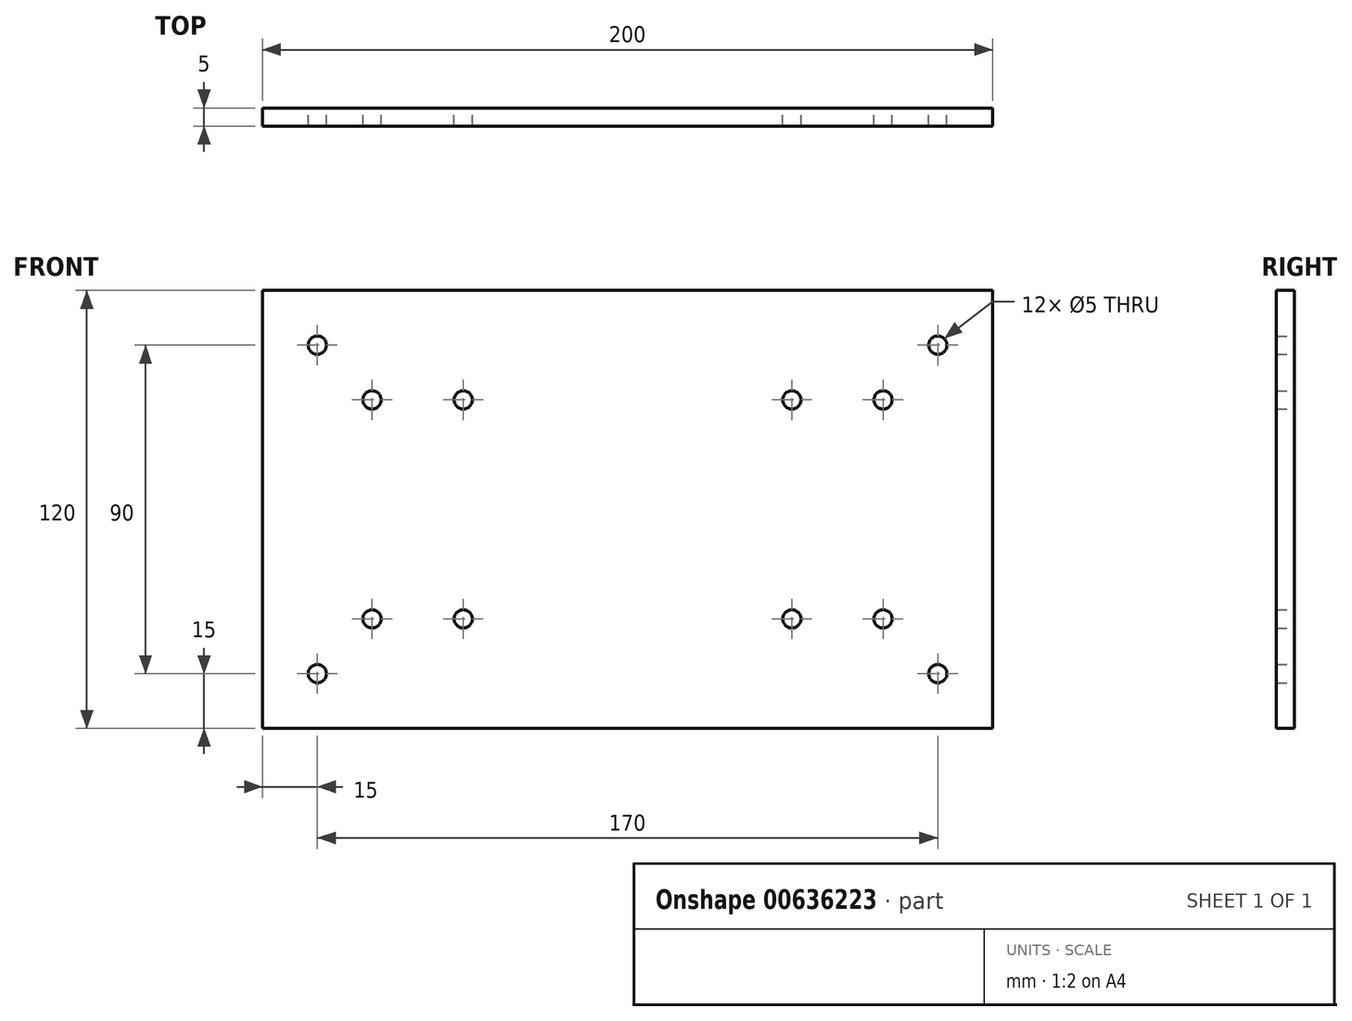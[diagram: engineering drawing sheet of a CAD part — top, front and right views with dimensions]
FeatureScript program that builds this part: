
annotation { "Feature Type Name" : "Feature", "Feature Type Description" : "" }
export const myFeature = defineFeature(function(context is Context, id is Id, definition is map)
    precondition{}
    {
        {
            var Q0;
            Q0=qCreatedBy(makeId("Front.planeOp"),FACE);
            var sketch = newSketch(context, id + "F0", { "sketchPlane" : qUnion([Q0])});
            skLineSegment(sketch, "E0.bottom", {"start": v(0, 0) * mm, "end": v(200, 0) * mm});
            skLineSegment(sketch, "E0.top", {"start": v(0, 120) * mm, "end": v(200, 120) * mm});
            skLineSegment(sketch, "E0.left", {"start": v(0, 0) * mm, "end": v(0, 120) * mm});
            skLineSegment(sketch, "E0.right", {"start": v(200, 0) * mm, "end": v(200, 120) * mm});
            skCircle(sketch, "E1", {"center": v(15, 105) * mm, "radius": 2.5 * mm});
            skCircle(sketch, "E2", {"center": v(30, 90) * mm, "radius": 2.5 * mm});
            skCircle(sketch, "E3", {"center": v(54.99, 90) * mm, "radius": 2.5 * mm});
            skCircle(sketch, "E4.MirrorC", {"center": v(185, 105) * mm, "radius": 2.5 * mm});
            skCircle(sketch, "E5.MirrorC", {"center": v(145.01, 90) * mm, "radius": 2.5 * mm});
            skCircle(sketch, "E6.MirrorC", {"center": v(170, 90) * mm, "radius": 2.5 * mm});
            skCircle(sketch, "E7.MirrorC", {"center": v(15, 15) * mm, "radius": 2.5 * mm});
            skCircle(sketch, "E8.MirrorC", {"center": v(30, 30) * mm, "radius": 2.5 * mm});
            skCircle(sketch, "E9.MirrorC", {"center": v(54.99, 30) * mm, "radius": 2.5 * mm});
            skCircle(sketch, "E10.MirrorC", {"center": v(145.01, 30) * mm, "radius": 2.5 * mm});
            skCircle(sketch, "E11.MirrorC", {"center": v(170, 30) * mm, "radius": 2.5 * mm});
            skCircle(sketch, "E12.MirrorC", {"center": v(185, 15) * mm, "radius": 2.5 * mm});
            skLineSegment(sketch, "E13", {"start": v(15, 15) * mm, "end": v(30, 30) * mm});
            skSolve(sketch);
        }
        {
            var Q0;
            Q0=makeQuery(id+"F0.imprint","IMPRINT",FACE,{"disambiguationData":[TD([[makeQuery(id+"F0.imprint","IMPRINT",EDGE,{"derivedFrom":sQuery(id+"F0.wireOp",EDGE,"E0.bottom")}),1.0]])]});
            extrude(context, id + "F1", {"entities" : qUnion([Q0]), "depth" : 5 * mm, "offsetDistance" : 25.4 * mm});
        }
    });
